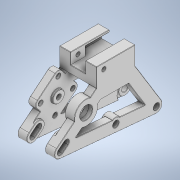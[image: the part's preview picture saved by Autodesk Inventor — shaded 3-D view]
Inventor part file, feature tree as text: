
AUTODESK INVENTOR PART (.ipt)
format: ipt  version: 2021 (Build 250183000, 183)  size: 1,145,344 bytes
history: native  units: mm
features: extrude x15, sketch x13, fillet x2, plane x1, mirror x1, projected_geometry x1
ambient origin geometry x8: Origin, YZ Plane, XZ Plane, XY Plane, X Axis, Y Axis, Z Axis, Center Point
bodies: Solid1 (feature_tree)
feature tree (33):
  extrude  "Extrusion1"  Depth=8.0mm
  sketch  "Sketch2"  dims[d3=75.0mm d4=5.0mm]
  extrude  "Extrusion2"  Depth=5.0mm
  extrude  "Extrusion3"  Depth=55.0mm
  extrude  "Extrusion4"  Depth=16.0mm
  plane  "Work Plane2"
  extrude  "Extrusion23"  Depth=16.0mm
  mirror  "Mirror2"
  extrude  "Extrusion24"  Depth=36.0mm
  extrude  "Extrusion25"  Depth=52.5mm
  extrude  "Extrusion26"  Depth=55.0mm
  sketch  "Sketch21"  dims[d21=26.25mm d22=55.0mm]
  extrude  "Extrusion27"  Depth=2.75mm TaperAngle=0.0deg
  extrude  "Extrusion28"  Depth=3.0mm TaperAngle=0.0deg
  extrude  "Extrusion29"  Depth=0.25mm TaperAngle=0.0deg
  extrude  "Extrusion30"  Depth=16.0mm
  extrude  "Extrusion31"  Depth=0.5mm
  extrude  "Extrusion37"  Depth=45.0mm
  extrude  "Extrusion36"  Depth=6.0mm
  fillet  "Fillet10"  Radius=36.0mm
  fillet  "Fillet11"  Radius=10.0mm
  sketch  "Sketch1"  dims[d0=8.0mm d1=8.0mm]
  sketch  "Sketch3"  dims[d7=8.0mm d8=55.0mm]
  sketch  "Sketch4"  dims[d9=7.0mm d12=16.0mm]
  projected_geometry  "Projected Loop1"
  sketch  "Sketch18"  dims[d13=16.0mm d14=16.0mm]
  sketch  "Sketch19"  dims[d15=22.0mm d16=36.0mm]
  sketch  "Sketch20"  dims[d17=40.0mm d20=52.5mm]
  sketch  "Sketch22"  dims[d26=10.0mm d27=0.0mm d28=2.75mm d29=0.0mm]
  sketch  "Sketch23"  dims[d30=26.0mm d31=3.0mm d32=0.0mm]
  sketch  "Sketch24"  dims[d34=16.0mm d35=0.25mm d36=0.0mm]
  sketch  "Sketch29"  dims[d37=12.25mm d55=16.0mm]
  sketch  "Sketch30"  dims[d56=0.5mm d57=0.5mm d58=45.0mm d61=6.0mm d62=36.0mm d63=10.0mm d64=8.0mm d65=4.0mm d164=50.0mm d165=0.0mm d166=50.0mm d167=0.0mm d168=25.0mm d169=0.0mm d170=32.0mm d171=12.75mm d172=0.0mm d173=22.0mm d174=7.0mm d175=0.0mm d176=17.0mm d177=0.0mm d178=0.0mm d179=15.5mm d180=15.5mm d181=3.0mm d182=6.0mm d183=13.0mm d184=40.0mm d186=360.0deg d188=10.0mm d189=0.0mm d190=10.0mm d191=0.0mm d192=3.0mm d193=0.0mm d194=22.0mm d195=2.0mm d196=0.0mm d204=0.0mm d205=0.0mm d233=15.0mm d234=2.5mm d235=12.5mm d236=5.0mm d237=15.0mm d238=2.5mm d239=12.5mm d240=5.0mm d241=0.5mm d242=0.5mm d246=5.0mm d247=10.0mm d248=7.5mm d249=0.0mm d250=0.0mm d261=40.0mm d262=2.5mm d263=20.0mm d264=15.0mm d265=0.0mm d266=0.5mm d267=0.5mm d223=0.5mm d224=0.872665mm d225=0.5mm d226=0.872665mm]
